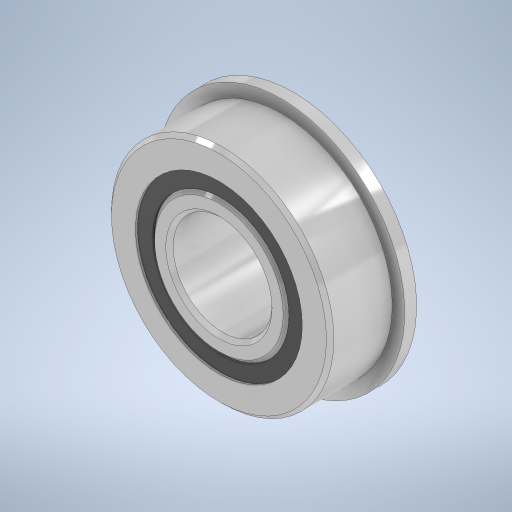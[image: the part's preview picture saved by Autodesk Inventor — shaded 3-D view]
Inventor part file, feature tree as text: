
AUTODESK INVENTOR PART (.ipt)
format: ipt  version: 2023 (Build 270158000, 158)  size: 761,856 bytes
history: native  units: in
note: dims shown in document units (in); Inventor stores cm internally (conversion verified against a paired STEP export)
features: other x12, revolve x4
ambient origin geometry x8: Origin, YZ Plane, XZ Plane, XY Plane, X Axis, Y Axis, Z Axis, Center Point
bodies: Solid1 (feature_tree), Solid2 (feature_tree), Solid3 (feature_tree), Solid4 (feature_tree), Solid5 (feature_tree), Solid6 (feature_tree), Solid7 (feature_tree), Solid8 (feature_tree), Solid9 (feature_tree), Solid10 (feature_tree), Solid11 (feature_tree), Solid12 (feature_tree), Solid13 (feature_tree), Solid14 (feature_tree), Solid15 (feature_tree), Solid16 (feature_tree)
feature tree (16):
  revolve  "Revolve4"  [1 undecoded]
  other  "CirPattern1[1]"
  other  "CirPattern1[2]"
  other  "CirPattern1[3]"
  other  "CirPattern1[4]"
  other  "CirPattern1[5]"
  other  "CirPattern1[6]"
  other  "CirPattern1[7]"
  other  "CirPattern1[8]"
  other  "CirPattern1[9]"
  other  "CirPattern1[10]"
  other  "CirPattern1[11]"
  revolve  "Revolve5[1]"  [1 undecoded]
  revolve  "Revolve5[2]"  [1 undecoded]
  revolve  "Revolve6"  [1 undecoded]
  other  "Cut-Extrude1"
note: 4 required parameter values undecoded (feature->parameter linkage not recoverable at this tier; creation-order binding heuristic only, values carry confidence <= 0.55)
